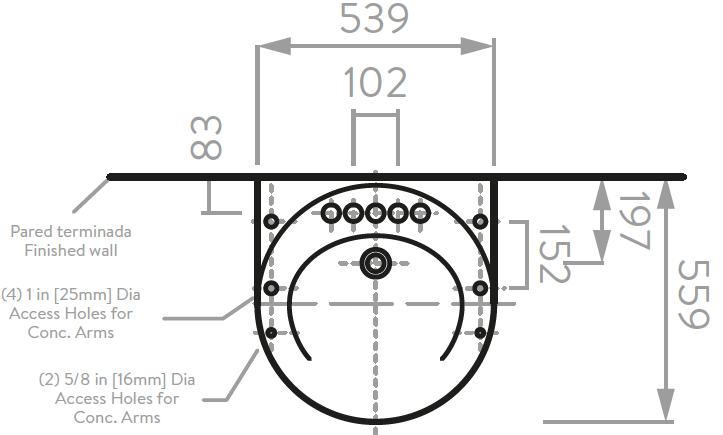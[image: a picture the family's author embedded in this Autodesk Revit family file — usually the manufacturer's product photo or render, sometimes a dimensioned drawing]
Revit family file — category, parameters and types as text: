
# Revit family: OO3891001_Lavamanos Free
name_source: partatom
category: Plumbing Fixtures
units: mm (PartAtom-declared; Revit-internal decimal feet)

## family parameters
Always vertical = Yes
Cut with Voids When Loaded = No
Host = Wall
OmniClass Number = 23.31.13.11
OmniClass Title = Single Sinks
Part Type = Normal
Room Calculation Point = No
Round Connector Dimension = Use Diameter
Shared = No

## types (1)
- Type 1
    Alto = 1000 mm  [stored 3.28084 ft]
    Ancho = 539 mm  [stored 1.76837 ft]
    Creado por = IDD
    Description = Lavamanos de colgar en porcelana con opción de pedestal que ofrece mayor estetica, seguridad y control de vandalismo, apto para destinos de alto tráfico e instituciones del sector público.
    Fecha de creación = 13/08/2020
    Garantía = Garantía Integral de por vida.
    Manufacturer = Corona
    Material = Corona_Porcelana_Sanitaria_Blanco
    Material Accesorios = Corona_Acero inoxidable
    Model = Free
    Normatividad Aplicada = ADA
    Peso = 17 Kg.
    Profundidad = 559 mm  [stored 1.83399 ft]
    Type Comments = Lavamanos de colgar
    URL = https://www.corona.co

note: [stored X ft] marks values corroborated as IEEE doubles in the binary element streams (Revit-internal decimal feet)

## geometry (parser evidence)
native form markers: Sweep x5
no freeform markers — native parametric forms only
